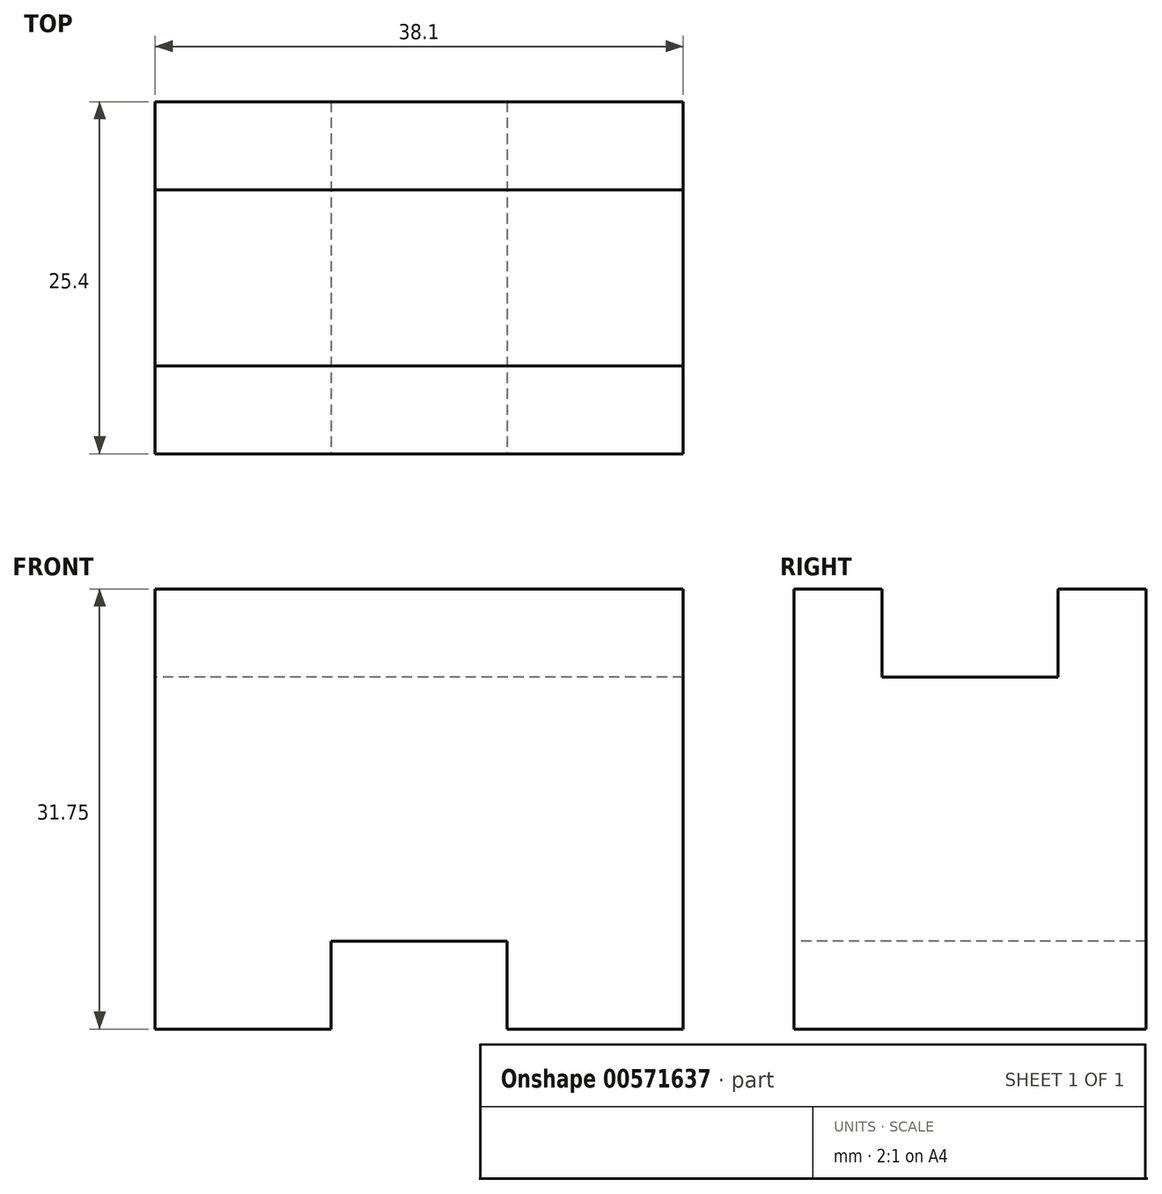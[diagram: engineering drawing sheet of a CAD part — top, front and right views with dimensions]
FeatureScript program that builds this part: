
annotation { "Feature Type Name" : "Feature", "Feature Type Description" : "" }
export const myFeature = defineFeature(function(context is Context, id is Id, definition is map)
    precondition{}
    {
        {
            var Q0;
            Q0=qCreatedBy(makeId("Front.planeOp"),FACE);
            var sketch = newSketch(context, id + "F0", { "sketchPlane" : qUnion([Q0])});
            skLineSegment(sketch, "E0", {"start": v(0, 0) * mm, "end": v(0, 31.75) * mm});
            skLineSegment(sketch, "E1", {"start": v(0, 31.75) * mm, "end": v(38.1, 31.75) * mm});
            skLineSegment(sketch, "E2", {"start": v(38.1, 31.75) * mm, "end": v(38.1, 0) * mm});
            skLineSegment(sketch, "E3", {"start": v(38.1, 0) * mm, "end": v(25.4, 0) * mm});
            skLineSegment(sketch, "E4", {"start": v(25.4, 0) * mm, "end": v(25.4, 6.35) * mm});
            skLineSegment(sketch, "E5", {"start": v(25.4, 6.35) * mm, "end": v(12.7, 6.35) * mm});
            skLineSegment(sketch, "E6", {"start": v(12.7, 6.35) * mm, "end": v(12.7, 0) * mm});
            skLineSegment(sketch, "E7", {"start": v(12.7, 0) * mm, "end": v(0, 0) * mm});
            skSolve(sketch);
        }
        {
            var Q0;
            Q0 = qSketchRegion(id + "F0", true);
            extrude(context, id + "F1", {"entities" : qUnion([Q0]), "oppositeDirection" : true, "depth" : 25.4 * mm, "offsetDistance" : 25.4 * mm});
        }
        {
            var Q0;
            Q0=makeQuery(id+"F1.opExtrude","SWEPT_FACE",FACE,{"disambiguationData":[OSD([sQuery(id+"F0.wireOp",EDGE,"E1")])]});
            var sketch = newSketch(context, id + "F2", { "sketchPlane" : qUnion([Q0])});
            skLineSegment(sketch, "E8", {"start": v(38.1, 0) * mm, "end": v(38.1, 6.35) * mm});
            skLineSegment(sketch, "E9", {"start": v(38.1, 6.35) * mm, "end": v(0, 6.35) * mm});
            skLineSegment(sketch, "E10", {"start": v(0, 6.35) * mm, "end": v(0, 19.05) * mm});
            skLineSegment(sketch, "E11", {"start": v(0, 19.05) * mm, "end": v(38.1, 19.05) * mm});
            skSolve(sketch);
        }
        {
            var Q0;
            Q0 = qSketchRegion(id + "F2", true);
            var Q1;
            {var subQ0=sQuery(id+"F2.wireOp",EDGE,"E9");Q1=makeQuery(id+"F2.imprint","IMPRINT",FACE,{"disambiguationData":[TD([[makeQuery(id+"F2.imprint","IMPRINT",EDGE,{"derivedFrom":subQ0}),-1.0]])]});}
            extrude(context, id + "F3", {"entities" : qUnion([Q0, Q1]), "operationType" : NewBodyOperationType.REMOVE, "oppositeDirection" : true, "depth" : 6.35 * mm, "offsetDistance" : 25.4 * mm});
        }
    });
